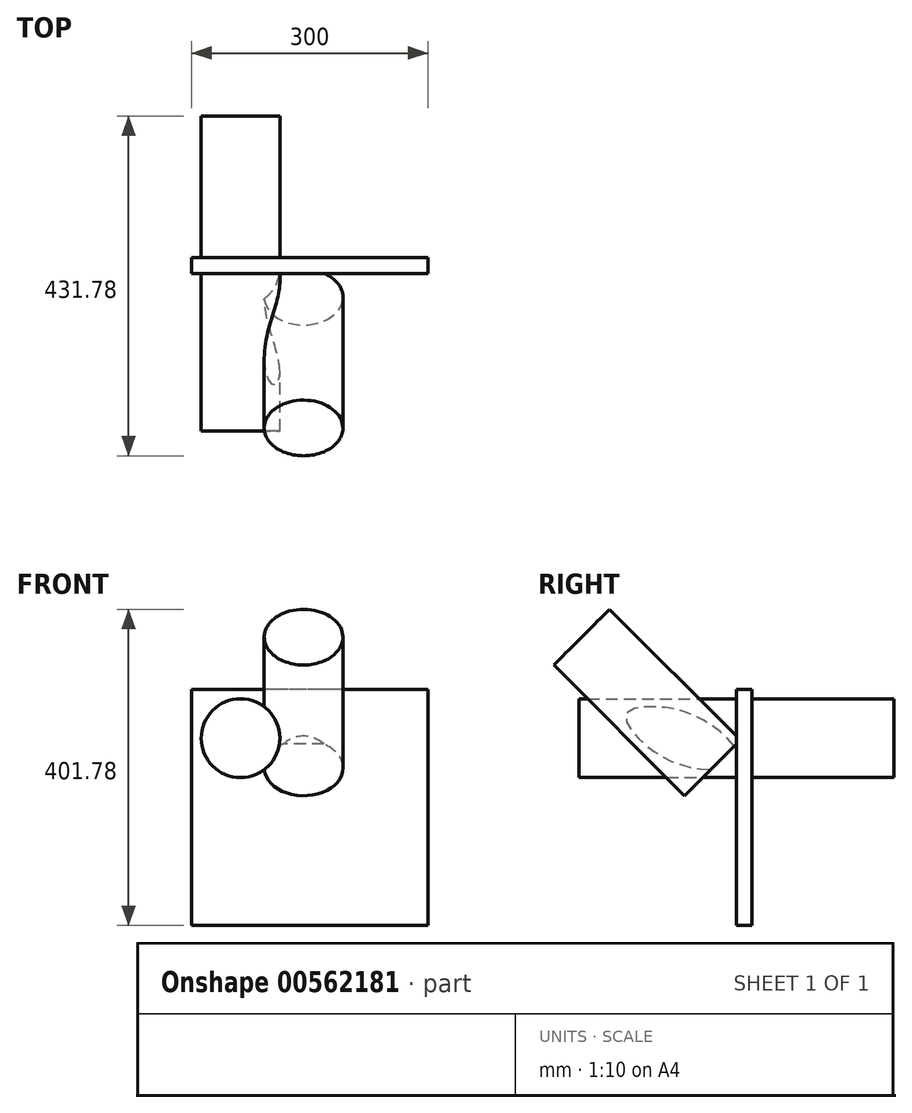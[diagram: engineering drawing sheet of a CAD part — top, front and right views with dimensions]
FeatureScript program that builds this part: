
annotation { "Feature Type Name" : "Feature", "Feature Type Description" : "" }
export const myFeature = defineFeature(function(context is Context, id is Id, definition is map)
    precondition{}
    {
        {
            var Q0;
            Q0=qCreatedBy(makeId("Front.planeOp"),FACE);
            var sketch = newSketch(context, id + "F0", { "sketchPlane" : qUnion([Q0])});
            skLineSegment(sketch, "E0.bottom", {"start": v(157.9, 150) * mm, "end": v(-142.1, 150) * mm});
            skLineSegment(sketch, "E0.top", {"start": v(157.9, -150) * mm, "end": v(-142.1, -150) * mm});
            skLineSegment(sketch, "E0.left", {"start": v(157.9, 150) * mm, "end": v(157.9, -150) * mm});
            skLineSegment(sketch, "E0.right", {"start": v(-142.1, 150) * mm, "end": v(-142.1, -150) * mm});
            skPoint(sketch, "E0.middle", {"position": v(7.9, 0) * mm});
            skSolve(sketch);
        }
        {
            var Q0;
            Q0 = qSketchRegion(id + "F0", true);
            extrude(context, id + "F1", {"entities" : qUnion([Q0]), "depth" : 20 * mm, "offsetDistance" : 25 * mm});
        }
        {
            var Q0;
            Q0=makeQuery(id+"F1.opExtrude","CAP_FACE",FACE,{"disambiguationData":[OSD([sQuery(id+"F0.wireOp",EDGE,"E0.bottom"),sQuery(id+"F0.wireOp",EDGE,"E0.top"),sQuery(id+"F0.wireOp",EDGE,"E0.left"),sQuery(id+"F0.wireOp",EDGE,"E0.right")])],"isStart":false});
            var sketch = newSketch(context, id + "F2", { "sketchPlane" : qUnion([Q0])});
            skCircle(sketch, "E1", {"center": v(-80.1, 88) * mm, "radius": 50 * mm});
            skSolve(sketch);
        }
        {
            var Q0;
            Q0=makeQuery(id+"F2.imprint","IMPRINT",FACE,{"disambiguationData":[TD([[makeQuery(id+"F2.imprint","IMPRINT",EDGE,{"derivedFrom":sQuery(id+"F2.wireOp",EDGE,"E1")}),1.0]])]});
            extrude(context, id + "F3", {"entities" : qUnion([Q0]), "operationType" : NewBodyOperationType.ADD, "depth" : 200 * mm, "offsetDistance" : 25 * mm, "hasSecondDirection" : true, "secondDirectionOppositeDirection" : true, "secondDirectionDepth" : 200 * mm});
        }
        {
            var Q0;
            Q0=makeQuery(id+"F1.opExtrude","CAP_EDGE",EDGE,{"disambiguationData":[OSD([sQuery(id+"F0.wireOp",EDGE,"E0.bottom")])],"isStart":true});
            cPlane(context, id + "F4", {"entities" : qUnion([Q0]), "cplaneType" : CPlaneType.LINE_ANGLE, "offset" : 25 * mm, "angle" : 45 * degree, "width" : 150 * mm, "height" : 150 * mm});
        }
        {
            var Q0;
            Q0=qCreatedBy(id+"F4.planeOp",FACE);
            var sketch = newSketch(context, id + "F5", { "sketchPlane" : qUnion([Q0])});
            skCircle(sketch, "E2", {"center": v(0, 0) * mm, "radius": 50 * mm});
            skSolve(sketch);
        }
        {
            var Q0;
            Q0 = qSketchRegion(id + "F5", true);
            extrude(context, id + "F6", {"entities" : qUnion([Q0]), "operationType" : NewBodyOperationType.ADD, "depth" : 200 * mm, "offsetDistance" : 25 * mm, "hasSecondDirection" : true, "secondDirectionOppositeDirection" : true, "secondDirectionDepth" : 35 * mm});
        }
    });
